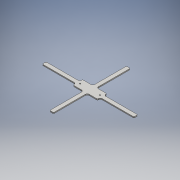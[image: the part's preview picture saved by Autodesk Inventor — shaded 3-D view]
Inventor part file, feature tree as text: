
AUTODESK INVENTOR PART (.ipt)
format: ipt  version: 2016 (Build 200138000, 138)  size: 155,136 bytes
history: native  units: mm
features: extrude x1, fillet x1, sketch x1
ambient origin geometry x8: Origin, YZ Plane, XZ Plane, XY Plane, X Axis, Y Axis, Z Axis, Center Point
bodies: Solid1 (feature_tree)
feature tree (3):
  extrude  "Extrusion1"  Depth=5.0mm
  fillet  "Fillet1"  Radius=10.0mm
  sketch  "Sketch1"  dims[d0=90.0mm d1=53.2mm d2=10.0mm d3=3.2mm d4=65.0mm d5=25.0mm d6=90.0mm d7=3.0mm d8=0.0mm d9=2.0mm d10=5.0mm]
